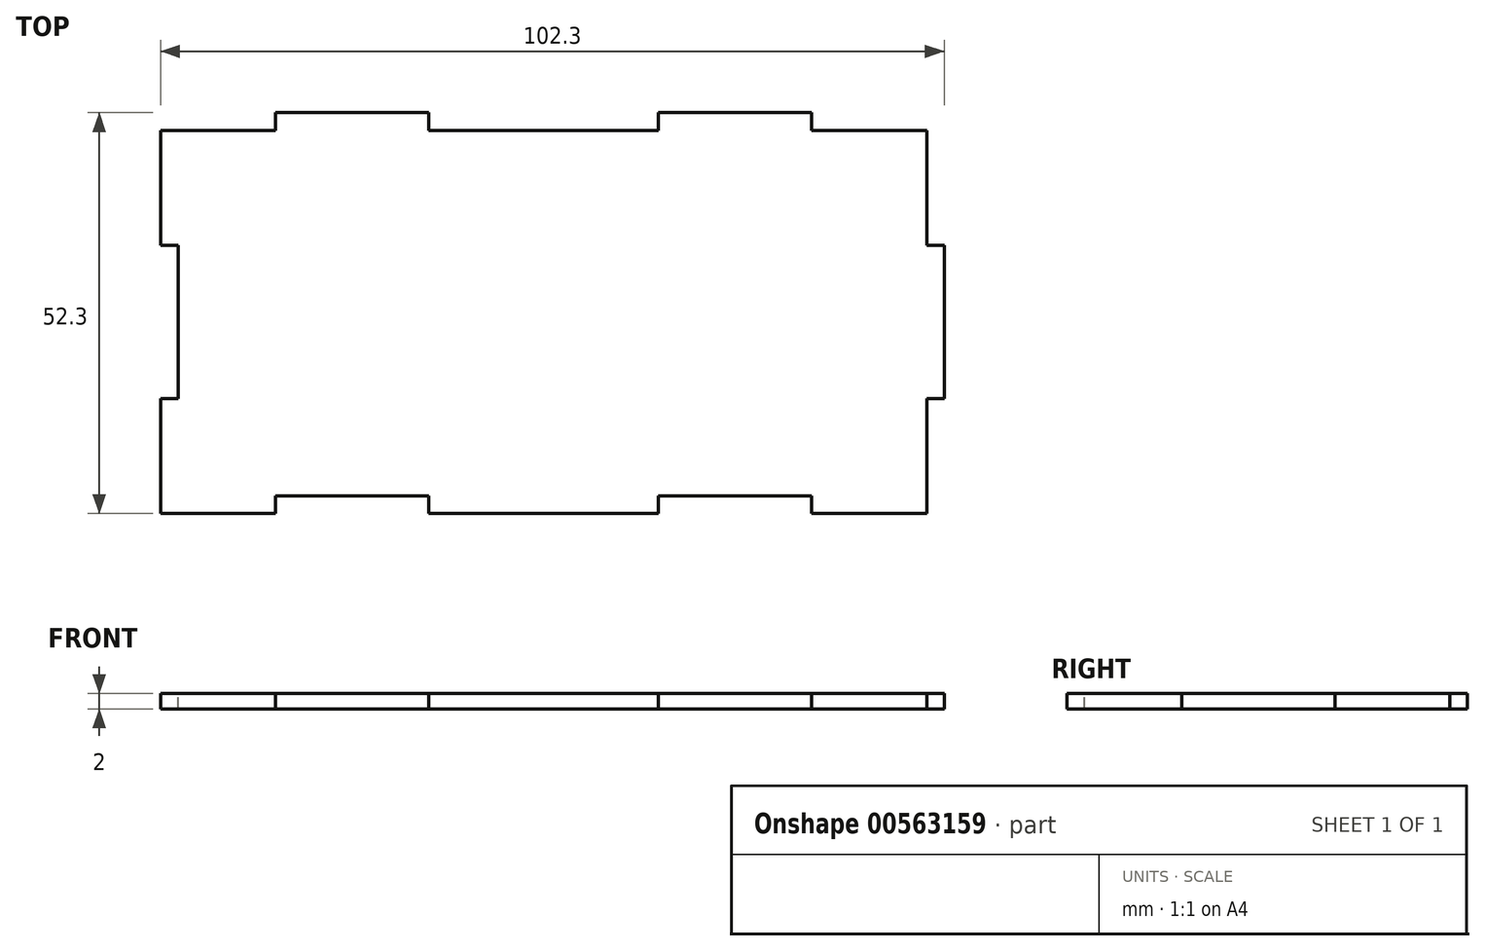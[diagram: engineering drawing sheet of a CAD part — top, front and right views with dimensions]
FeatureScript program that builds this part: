
annotation { "Feature Type Name" : "Feature", "Feature Type Description" : "" }
export const myFeature = defineFeature(function(context is Context, id is Id, definition is map)
    precondition{}
    {
        {
            var Q0;
            Q0=qCreatedBy(makeId("Top.planeOp"),FACE);
            var sketch = newSketch(context, id + "F0", { "sketchPlane" : qUnion([Q0])});
            skLineSegment(sketch, "E0.bottom", {"start": v(-54.67, 39.9) * mm, "end": v(45.33, 39.9) * mm});
            skLineSegment(sketch, "E0.top", {"start": v(-54.67, -10.1) * mm, "end": v(45.33, -10.1) * mm});
            skLineSegment(sketch, "E0.left", {"start": v(-54.67, 39.9) * mm, "end": v(-54.67, -10.1) * mm});
            skLineSegment(sketch, "E0.right", {"start": v(45.33, 39.9) * mm, "end": v(45.33, -10.1) * mm});
            skLineSegment(sketch, "E1.bottom", {"start": v(-39.67, 39.9) * mm, "end": v(-19.67, 39.9) * mm});
            skLineSegment(sketch, "E1.top", {"start": v(-39.67, 42.2) * mm, "end": v(-19.67, 42.2) * mm});
            skLineSegment(sketch, "E1.left", {"start": v(-39.67, 39.9) * mm, "end": v(-39.67, 42.2) * mm});
            skLineSegment(sketch, "E1.right", {"start": v(-19.67, 39.9) * mm, "end": v(-19.67, 42.2) * mm});
            skLineSegment(sketch, "E2.bottom", {"start": v(30.33, 39.9) * mm, "end": v(10.33, 39.9) * mm});
            skLineSegment(sketch, "E2.top", {"start": v(30.33, 42.2) * mm, "end": v(10.33, 42.2) * mm});
            skLineSegment(sketch, "E2.left", {"start": v(30.33, 39.9) * mm, "end": v(30.33, 42.2) * mm});
            skLineSegment(sketch, "E2.right", {"start": v(10.33, 39.9) * mm, "end": v(10.33, 42.2) * mm});
            skLineSegment(sketch, "E3.bottom", {"start": v(45.33, 24.9) * mm, "end": v(47.63, 24.9) * mm});
            skLineSegment(sketch, "E3.top", {"start": v(45.33, 4.9) * mm, "end": v(47.63, 4.9) * mm});
            skLineSegment(sketch, "E3.left", {"start": v(45.33, 24.9) * mm, "end": v(45.33, 4.9) * mm});
            skLineSegment(sketch, "E3.right", {"start": v(47.63, 24.9) * mm, "end": v(47.63, 4.9) * mm});
            skSolve(sketch);
        }
        {
            var Q0;
            Q0 = qSketchRegion(id + "F0", true);
            extrude(context, id + "F1", {"entities" : qUnion([Q0]), "depth" : 2 * mm, "offsetDistance" : 25 * mm});
        }
        {
            var Q0;
            Q0=makeQuery(id+"F1.opExtrude","CAP_FACE",FACE,{"disambiguationData":[OSD([sQuery(id+"F0.wireOp",EDGE,"E0.bottom"),sQuery(id+"F0.wireOp",EDGE,"E0.top"),sQuery(id+"F0.wireOp",EDGE,"E0.left"),sQuery(id+"F0.wireOp",EDGE,"E0.right"),sQuery(id+"F0.wireOp",EDGE,"E1.top"),sQuery(id+"F0.wireOp",EDGE,"E1.left"),sQuery(id+"F0.wireOp",EDGE,"E1.right"),sQuery(id+"F0.wireOp",EDGE,"E2.top"),sQuery(id+"F0.wireOp",EDGE,"E2.left"),sQuery(id+"F0.wireOp",EDGE,"E2.right")])],"isStart":false});
            var sketch = newSketch(context, id + "F2", { "sketchPlane" : qUnion([Q0])});
            skLineSegment(sketch, "E4.bottom", {"start": v(-39.67, -10.1) * mm, "end": v(-19.67, -10.1) * mm});
            skLineSegment(sketch, "E4.top", {"start": v(-39.67, -7.8) * mm, "end": v(-19.67, -7.8) * mm});
            skLineSegment(sketch, "E4.left", {"start": v(-39.67, -10.1) * mm, "end": v(-39.67, -7.8) * mm});
            skLineSegment(sketch, "E4.right", {"start": v(-19.67, -10.1) * mm, "end": v(-19.67, -7.8) * mm});
            skLineSegment(sketch, "E5.bottom", {"start": v(30.33, -10.1) * mm, "end": v(10.33, -10.1) * mm});
            skLineSegment(sketch, "E5.top", {"start": v(30.33, -7.8) * mm, "end": v(10.33, -7.8) * mm});
            skLineSegment(sketch, "E5.left", {"start": v(30.33, -10.1) * mm, "end": v(30.33, -7.8) * mm});
            skLineSegment(sketch, "E5.right", {"start": v(10.33, -10.1) * mm, "end": v(10.33, -7.8) * mm});
            skLineSegment(sketch, "E6.bottom", {"start": v(-54.67, 24.9) * mm, "end": v(-52.37, 24.9) * mm});
            skLineSegment(sketch, "E6.top", {"start": v(-54.67, 4.9) * mm, "end": v(-52.37, 4.9) * mm});
            skLineSegment(sketch, "E6.left", {"start": v(-54.67, 24.9) * mm, "end": v(-54.67, 4.9) * mm});
            skLineSegment(sketch, "E6.right", {"start": v(-52.37, 24.9) * mm, "end": v(-52.37, 4.9) * mm});
            skSolve(sketch);
        }
        {
            var Q0;
            Q0 = qSketchRegion(id + "F2", true);
            extrude(context, id + "F3", {"entities" : qUnion([Q0]), "operationType" : NewBodyOperationType.REMOVE, "oppositeDirection" : true, "depth" : 5 * mm, "offsetDistance" : 25 * mm});
        }
    });
